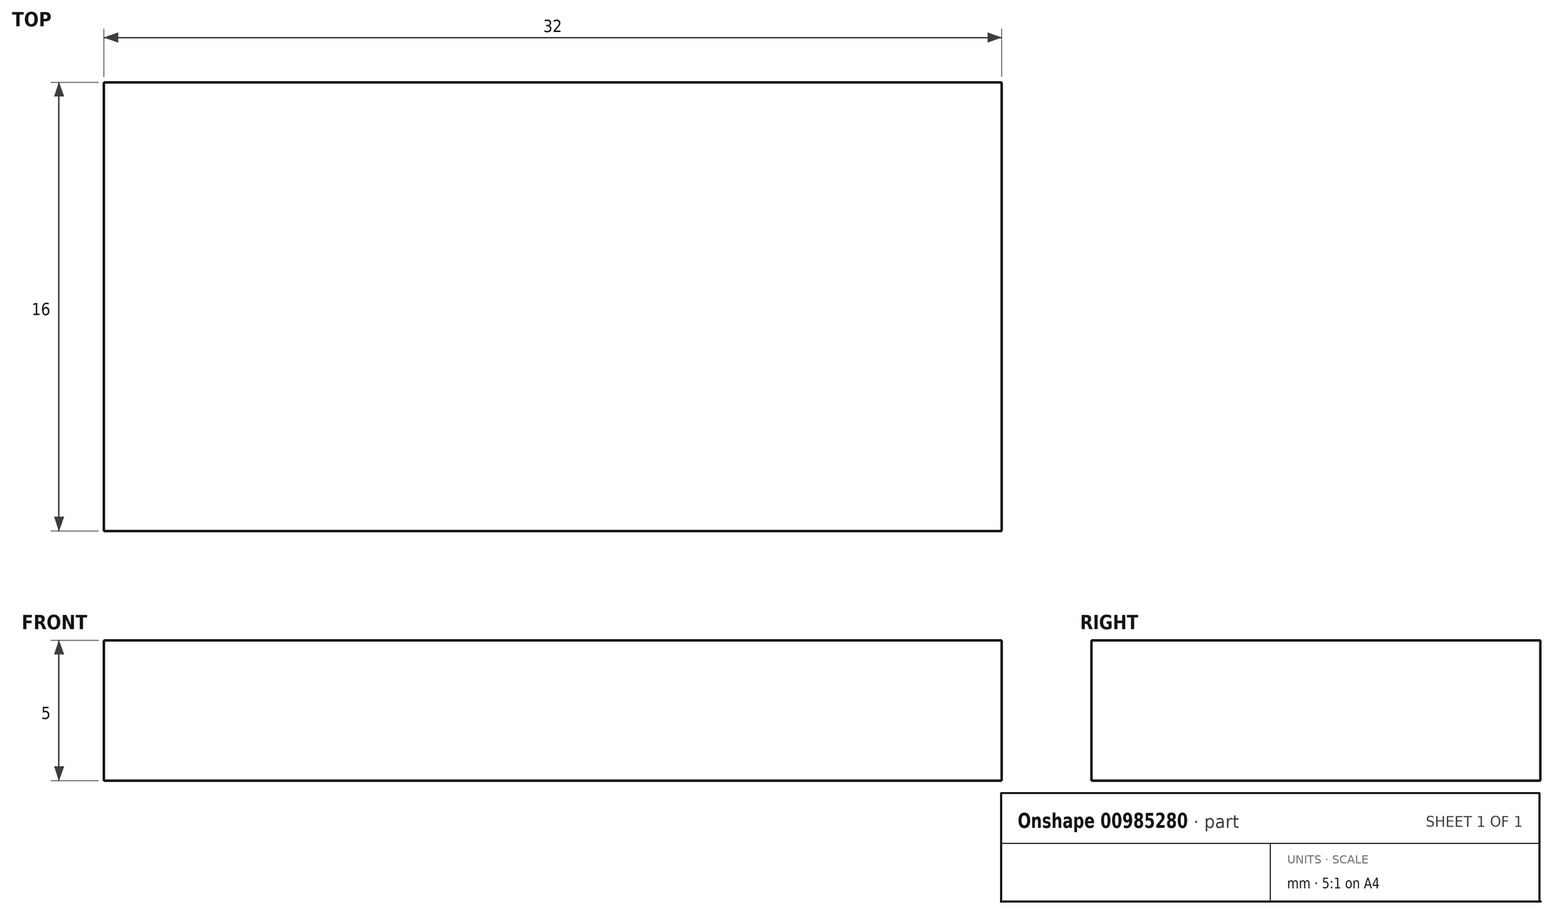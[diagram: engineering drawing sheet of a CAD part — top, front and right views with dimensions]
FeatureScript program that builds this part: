
annotation { "Feature Type Name" : "Feature", "Feature Type Description" : "" }
export const myFeature = defineFeature(function(context is Context, id is Id, definition is map)
    precondition{}
    {
        {
            var Q0;
            Q0=qCreatedBy(makeId("Top.planeOp"),FACE);
            var sketch = newSketch(context, id + "F0", { "sketchPlane" : qUnion([Q0])});
            skLineSegment(sketch, "E0.bottom", {"start": v(0, 0) * mm, "end": v(32, 0) * mm});
            skLineSegment(sketch, "E0.top", {"start": v(0, 16) * mm, "end": v(32, 16) * mm});
            skLineSegment(sketch, "E0.left", {"start": v(0, 0) * mm, "end": v(0, 16) * mm});
            skLineSegment(sketch, "E0.right", {"start": v(32, 0) * mm, "end": v(32, 16) * mm});
            skSolve(sketch);
        }
        {
            var Q0;
            Q0=makeQuery(id+"F0.imprint","IMPRINT",FACE,{"disambiguationData":[TD([[makeQuery(id+"F0.imprint","IMPRINT",EDGE,{"derivedFrom":sQuery(id+"F0.wireOp",EDGE,"E0.bottom")}),1.0]])]});
            extrude(context, id + "F1", {"entities" : qUnion([Q0]), "depth" : 5 * mm, "offsetDistance" : 25.4 * mm});
        }
        {
            var Q0;
            Q0=makeQuery(id+"F1.opExtrude","CAP_FACE",FACE,{"disambiguationData":[OSD([sQuery(id+"F0.wireOp",EDGE,"E0.bottom"),sQuery(id+"F0.wireOp",EDGE,"E0.top"),sQuery(id+"F0.wireOp",EDGE,"E0.left"),sQuery(id+"F0.wireOp",EDGE,"E0.right")])],"isStart":false});
            var sketch = newSketch(context, id + "F2", { "sketchPlane" : qUnion([Q0])});
            skCircle(sketch, "E1", {"center": v(3.9, 12.1) * mm, "radius": 2.35 * mm});
            skCircle(sketch, "E2.0.1.0", {"center": v(3.9, 4.1) * mm, "radius": 2.35 * mm});
            skCircle(sketch, "E2.1.0.0", {"center": v(11.9, 12.1) * mm, "radius": 2.35 * mm});
            skCircle(sketch, "E2.1.1.0", {"center": v(11.9, 4.1) * mm, "radius": 2.35 * mm});
            skCircle(sketch, "E2.2.0.0", {"center": v(19.9, 12.1) * mm, "radius": 2.35 * mm});
            skCircle(sketch, "E2.2.1.0", {"center": v(19.9, 4.1) * mm, "radius": 2.35 * mm});
            skCircle(sketch, "E2.3.0.0", {"center": v(27.9, 12.1) * mm, "radius": 2.35 * mm});
            skCircle(sketch, "E2.3.1.0", {"center": v(27.9, 4.1) * mm, "radius": 2.35 * mm});
            skLineSegment(sketch, "E2.direction1", {"start": v(3.9, 12.1) * mm, "end": v(11.9, 12.1) * mm, "construction": true});
            skLineSegment(sketch, "E2.direction2", {"start": v(3.9, 12.1) * mm, "end": v(3.9, 4.1) * mm, "construction": true});
            skSolve(sketch);
        }
        {
            var Q0;
            Q0=sQuery(id+"F2.wireOp",EDGE,"E1");
            var Q1;
            Q1=sQuery(id+"F2.wireOp",EDGE,"E2.0.1.0");
            var Q2;
            Q2=sQuery(id+"F2.wireOp",EDGE,"E2.1.0.0");
            var Q3;
            Q3=sQuery(id+"F2.wireOp",EDGE,"E2.1.1.0");
            var Q4;
            Q4=sQuery(id+"F2.wireOp",EDGE,"E2.2.0.0");
            var Q5;
            Q5=sQuery(id+"F2.wireOp",EDGE,"E2.2.1.0");
            var Q6;
            Q6=sQuery(id+"F2.wireOp",EDGE,"E2.3.1.0");
            var Q7;
            Q7=sQuery(id+"F2.wireOp",EDGE,"E2.3.0.0");
            extrude(context, id + "F3", {"bodyType" : ToolBodyType.SURFACE, "surfaceEntities" : qUnion([Q0, Q1, Q2, Q3, Q4, Q5, Q6, Q7]), "depth" : 1.85 * mm, "offsetDistance" : 25.4 * mm});
        }
    });
